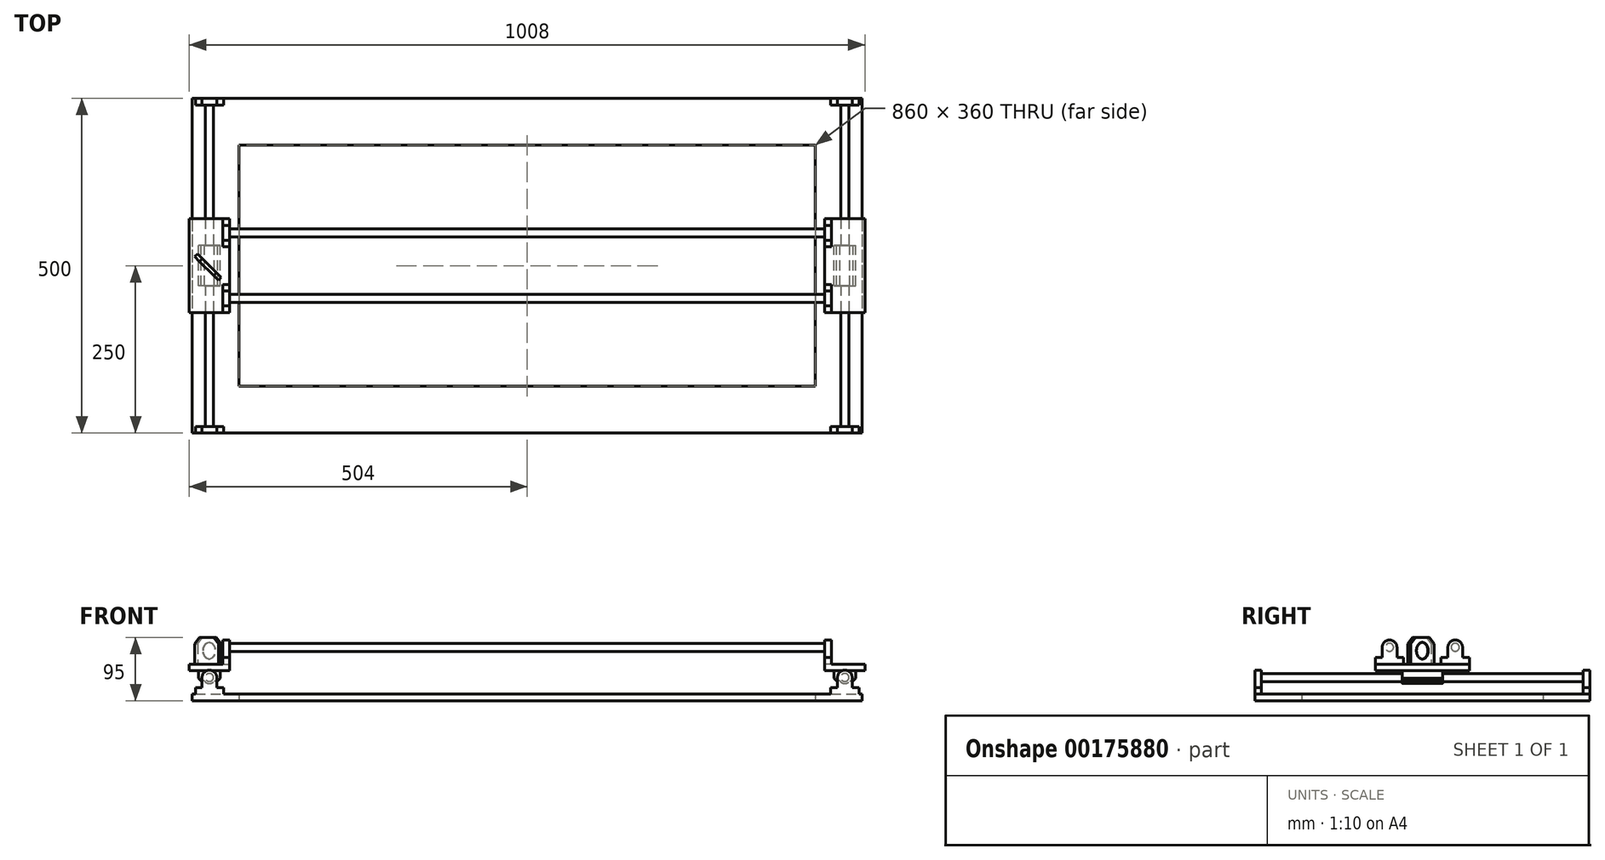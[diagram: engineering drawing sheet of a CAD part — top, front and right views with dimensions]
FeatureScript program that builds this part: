
annotation { "Feature Type Name" : "Feature", "Feature Type Description" : "" }
export const myFeature = defineFeature(function(context is Context, id is Id, definition is map)
    precondition{}
    {
        {
            var Q0;
            Q0=qCreatedBy(makeId("Top.planeOp"),FACE);
            var sketch = newSketch(context, id + "F0", { "sketchPlane" : qUnion([Q0])});
            skLineSegment(sketch, "E0.bottom", {"start": v(-500, 250) * mm, "end": v(500, 250) * mm});
            skLineSegment(sketch, "E0.top", {"start": v(-500, -250) * mm, "end": v(500, -250) * mm});
            skLineSegment(sketch, "E0.left", {"start": v(-500, 250) * mm, "end": v(-500, -250) * mm});
            skLineSegment(sketch, "E0.right", {"start": v(500, 250) * mm, "end": v(500, -250) * mm});
            skPoint(sketch, "E0.middle", {"position": v(0, 0) * mm});
            skLineSegment(sketch, "E1.0", {"start": v(-430, 180) * mm, "end": v(430, 180) * mm});
            skLineSegment(sketch, "E1.1", {"start": v(-430, 180) * mm, "end": v(-430, -180) * mm});
            skLineSegment(sketch, "E1.2", {"start": v(-430, -180) * mm, "end": v(430, -180) * mm});
            skLineSegment(sketch, "E1.3", {"start": v(430, 180) * mm, "end": v(430, -180) * mm});
            skSolve(sketch);
        }
        {
            var Q0;
            Q0=makeQuery(id+"F0.imprint","IMPRINT",FACE,{"disambiguationData":[TD([[makeQuery(id+"F0.imprint","IMPRINT",EDGE,{"derivedFrom":sQuery(id+"F0.wireOp",EDGE,"E0.bottom")}),-1.0]])]});
            extrude(context, id + "F1", {"entities" : qUnion([Q0]), "endBound" : BoundingType.SYMMETRIC, "depth" : 10 * mm});
        }
        {
            var Q0;
            Q0=makeQuery(id+"F1.opExtrude","SWEPT_FACE",FACE,{"disambiguationData":[OSD([sQuery(id+"F0.wireOp",EDGE,"E0.top")])]});
            var sketch = newSketch(context, id + "F2", { "sketchPlane" : qUnion([Q0])});
            skCircle(sketch, "E2", {"center": v(-474, 30) * mm, "radius": 6 * mm});
            skArc(sketch, "E3", {"start": v(-485, 30) * mm, "mid": v(-481.78, 37.78) * mm, "end": v(-474, 41) * mm});
            skLineSegment(sketch, "E4", {"start": v(-485, 30) * mm, "end": v(-485, 15) * mm});
            skLineSegment(sketch, "E5", {"start": v(-485, 15) * mm, "end": v(-495, 15) * mm});
            skLineSegment(sketch, "E6", {"start": v(-495, 15) * mm, "end": v(-495, 5) * mm});
            skLineSegment(sketch, "E7", {"start": v(-474, 30) * mm, "end": v(-474, 5) * mm, "construction": true});
            skArc(sketch, "E8.MirrorCS", {"start": v(-463, 30) * mm, "mid": v(-466.22, 37.78) * mm, "end": v(-474, 41) * mm});
            skLineSegment(sketch, "E9.MirrorCS", {"start": v(-463, 30) * mm, "end": v(-463, 15) * mm});
            skLineSegment(sketch, "E10.MirrorCS", {"start": v(-453, 15) * mm, "end": v(-453, 5) * mm});
            skLineSegment(sketch, "E11.MirrorCS", {"start": v(-463, 15) * mm, "end": v(-453, 15) * mm});
            skLineSegment(sketch, "E12", {"start": v(-495, 5) * mm, "end": v(-453, 5) * mm});
            skCircle(sketch, "E13.MirrorC", {"center": v(474, 30) * mm, "radius": 6 * mm});
            skArc(sketch, "E14.MirrorCS", {"start": v(463, 30) * mm, "mid": v(466.22, 37.78) * mm, "end": v(474, 41) * mm});
            skLineSegment(sketch, "E15.MirrorCS", {"start": v(453, 15) * mm, "end": v(453, 5) * mm});
            skLineSegment(sketch, "E16.MirrorCS", {"start": v(463, 30) * mm, "end": v(463, 15) * mm});
            skLineSegment(sketch, "E17.MirrorCS", {"start": v(485, 15) * mm, "end": v(495, 15) * mm});
            skLineSegment(sketch, "E18.MirrorCS", {"start": v(495, 15) * mm, "end": v(495, 5) * mm});
            skLineSegment(sketch, "E19.MirrorCS", {"start": v(485, 30) * mm, "end": v(485, 15) * mm});
            skArc(sketch, "E20.MirrorCS", {"start": v(485, 30) * mm, "mid": v(481.78, 37.78) * mm, "end": v(474, 41) * mm});
            skLineSegment(sketch, "E21.MirrorCS", {"start": v(463, 15) * mm, "end": v(453, 15) * mm});
            skLineSegment(sketch, "E22.MirrorCS", {"start": v(474, 30) * mm, "end": v(474, 5) * mm, "construction": true});
            skLineSegment(sketch, "E23.MirrorCS", {"start": v(495, 5) * mm, "end": v(453, 5) * mm});
            skSolve(sketch);
        }
        {
            var Q0;
            Q0 = qSketchRegion(id + "F2", true);
            extrude(context, id + "F3", {"entities" : qUnion([Q0]), "oppositeDirection" : true, "depth" : 10 * mm});
        }
        {
            var Q0;
            Q0=makeQuery(id+"F3.opExtrude","SWEPT_BODY",BODY,{"disambiguationData":[OSD([sQuery(id+"F2.wireOp",EDGE,"E2"),sQuery(id+"F2.wireOp",EDGE,"E3"),sQuery(id+"F2.wireOp",EDGE,"E4"),sQuery(id+"F2.wireOp",EDGE,"E5"),sQuery(id+"F2.wireOp",EDGE,"E6"),sQuery(id+"F2.wireOp",EDGE,"E8.MirrorCS"),sQuery(id+"F2.wireOp",EDGE,"E9.MirrorCS"),sQuery(id+"F2.wireOp",EDGE,"E10.MirrorCS"),sQuery(id+"F2.wireOp",EDGE,"E11.MirrorCS"),sQuery(id+"F2.wireOp",EDGE,"E12")])]});
            var Q1;
            Q1=makeQuery(id+"F3.opExtrude","SWEPT_BODY",BODY,{"disambiguationData":[OSD([sQuery(id+"F2.wireOp",EDGE,"E13.MirrorC"),sQuery(id+"F2.wireOp",EDGE,"E14.MirrorCS"),sQuery(id+"F2.wireOp",EDGE,"E15.MirrorCS"),sQuery(id+"F2.wireOp",EDGE,"E16.MirrorCS"),sQuery(id+"F2.wireOp",EDGE,"E17.MirrorCS"),sQuery(id+"F2.wireOp",EDGE,"E18.MirrorCS"),sQuery(id+"F2.wireOp",EDGE,"E19.MirrorCS"),sQuery(id+"F2.wireOp",EDGE,"E20.MirrorCS"),sQuery(id+"F2.wireOp",EDGE,"E21.MirrorCS"),sQuery(id+"F2.wireOp",EDGE,"E23.MirrorCS")])]});
            var Q2;
            Q2=qCreatedBy(makeId("Front.planeOp"),FACE);
            mirror(context, id + "F4", {"operationType" : NewBodyOperationType.ADD, "entities" : qUnion([Q0, Q1]), "mirrorPlane" : qUnion([Q2])});
        }
        {
            var Q0;
            Q0=makeQuery(id+"F4.boolean.opBoolean","MERGE",FACE,{"derivedFrom":[makeQuery(id+"F1.opExtrude","SWEPT_FACE",FACE,{"disambiguationData":[OSD([sQuery(id+"F0.wireOp",EDGE,"E0.top")])]}),makeQuery(id+"F3.opExtrude","CAP_FACE",FACE,{"disambiguationData":[OSD([sQuery(id+"F2.wireOp",EDGE,"E2"),sQuery(id+"F2.wireOp",EDGE,"E3"),sQuery(id+"F2.wireOp",EDGE,"E4"),sQuery(id+"F2.wireOp",EDGE,"E5"),sQuery(id+"F2.wireOp",EDGE,"E6"),sQuery(id+"F2.wireOp",EDGE,"E8.MirrorCS"),sQuery(id+"F2.wireOp",EDGE,"E9.MirrorCS"),sQuery(id+"F2.wireOp",EDGE,"E10.MirrorCS"),sQuery(id+"F2.wireOp",EDGE,"E11.MirrorCS"),sQuery(id+"F2.wireOp",EDGE,"E12")])],"isStart":true}),makeQuery(id+"F3.opExtrude","CAP_FACE",FACE,{"disambiguationData":[OSD([sQuery(id+"F2.wireOp",EDGE,"E13.MirrorC"),sQuery(id+"F2.wireOp",EDGE,"E14.MirrorCS"),sQuery(id+"F2.wireOp",EDGE,"E15.MirrorCS"),sQuery(id+"F2.wireOp",EDGE,"E16.MirrorCS"),sQuery(id+"F2.wireOp",EDGE,"E17.MirrorCS"),sQuery(id+"F2.wireOp",EDGE,"E18.MirrorCS"),sQuery(id+"F2.wireOp",EDGE,"E19.MirrorCS"),sQuery(id+"F2.wireOp",EDGE,"E20.MirrorCS"),sQuery(id+"F2.wireOp",EDGE,"E21.MirrorCS"),sQuery(id+"F2.wireOp",EDGE,"E23.MirrorCS")])],"isStart":true})]});
            var sketch = newSketch(context, id + "F5", { "sketchPlane" : qUnion([Q0])});
            skCircle(sketch, "E24.0", {"center": v(-474, 30) * mm, "radius": 6 * mm});
            skCircle(sketch, "E25.0", {"center": v(474, 30) * mm, "radius": 6 * mm});
            skSolve(sketch);
        }
        {
            var Q0;
            Q0 = qSketchRegion(id + "F5", true);
            var Q1;
            Q1=makeQuery(id+"F4.boolean.opBoolean","MERGE",FACE,{"derivedFrom":[makeQuery(id+"F1.opExtrude","SWEPT_FACE",FACE,{"disambiguationData":[OSD([sQuery(id+"F0.wireOp",EDGE,"E0.bottom")])]}),makeQuery(id+"F4.opPattern","COPY",FACE,{"derivedFrom":makeQuery(id+"F3.opExtrude","CAP_FACE",FACE,{"disambiguationData":[OSD([sQuery(id+"F2.wireOp",EDGE,"E2"),sQuery(id+"F2.wireOp",EDGE,"E3"),sQuery(id+"F2.wireOp",EDGE,"E4"),sQuery(id+"F2.wireOp",EDGE,"E5"),sQuery(id+"F2.wireOp",EDGE,"E6"),sQuery(id+"F2.wireOp",EDGE,"E8.MirrorCS"),sQuery(id+"F2.wireOp",EDGE,"E9.MirrorCS"),sQuery(id+"F2.wireOp",EDGE,"E10.MirrorCS"),sQuery(id+"F2.wireOp",EDGE,"E11.MirrorCS"),sQuery(id+"F2.wireOp",EDGE,"E12")])],"isStart":true}),"instanceName":"1"}),makeQuery(id+"F4.opPattern","COPY",FACE,{"derivedFrom":makeQuery(id+"F3.opExtrude","CAP_FACE",FACE,{"disambiguationData":[OSD([sQuery(id+"F2.wireOp",EDGE,"E13.MirrorC"),sQuery(id+"F2.wireOp",EDGE,"E14.MirrorCS"),sQuery(id+"F2.wireOp",EDGE,"E15.MirrorCS"),sQuery(id+"F2.wireOp",EDGE,"E16.MirrorCS"),sQuery(id+"F2.wireOp",EDGE,"E17.MirrorCS"),sQuery(id+"F2.wireOp",EDGE,"E18.MirrorCS"),sQuery(id+"F2.wireOp",EDGE,"E19.MirrorCS"),sQuery(id+"F2.wireOp",EDGE,"E20.MirrorCS"),sQuery(id+"F2.wireOp",EDGE,"E21.MirrorCS"),sQuery(id+"F2.wireOp",EDGE,"E23.MirrorCS")])],"isStart":true}),"instanceName":"1"})]});
            extrude(context, id + "F6", {"entities" : qUnion([Q0]), "operationType" : NewBodyOperationType.ADD, "endBound" : BoundingType.UP_TO_SURFACE, "oppositeDirection" : true, "endBoundEntityFace" : qUnion([Q1]), "depth" : 353 * mm});
        }
        {
            var Q0;
            Q0=qCreatedBy(makeId("Front.planeOp"),FACE);
            var sketch = newSketch(context, id + "F7", { "sketchPlane" : qUnion([Q0])});
            skCircle(sketch, "E26.0", {"center": v(-474, 30) * mm, "radius": 6 * mm, "construction": true});
            skArc(sketch, "E27", {"start": v(-466.54, 24.97) * mm, "mid": v(-469.77, 22.05) * mm, "end": v(-474, 21) * mm});
            skLineSegment(sketch, "E28", {"start": v(-466.54, 24.97) * mm, "end": v(-461.54, 24.97) * mm});
            skLineSegment(sketch, "E29", {"start": v(-461.54, 24.97) * mm, "end": v(-458, 28.5) * mm});
            skLineSegment(sketch, "E30", {"start": v(-458, 28.5) * mm, "end": v(-458, 40) * mm});
            skLineSegment(sketch, "E31", {"start": v(-458, 40) * mm, "end": v(-474, 40) * mm});
            skLineSegment(sketch, "E32", {"start": v(-474, 21) * mm, "end": v(-474, 40) * mm, "construction": true});
            skLineSegment(sketch, "E33.MirrorCS", {"start": v(-481.46, 24.97) * mm, "end": v(-486.46, 24.97) * mm});
            skLineSegment(sketch, "E34.MirrorCS", {"start": v(-486.46, 24.97) * mm, "end": v(-490, 28.5) * mm});
            skArc(sketch, "E35.MirrorCS", {"start": v(-481.46, 24.97) * mm, "mid": v(-478.23, 22.05) * mm, "end": v(-474, 21) * mm});
            skLineSegment(sketch, "E36.MirrorCS", {"start": v(-490, 28.5) * mm, "end": v(-490, 40) * mm});
            skLineSegment(sketch, "E37.MirrorCS", {"start": v(-490, 40) * mm, "end": v(-474, 40) * mm});
            skSolve(sketch);
        }
        {
            var Q0;
            Q0 = qSketchRegion(id + "F7", true);
            extrude(context, id + "F8", {"entities" : qUnion([Q0]), "endBound" : BoundingType.SYMMETRIC, "depth" : 60 * mm});
        }
        {
            var Q0;
            Q0=makeQuery(id+"F8.opExtrude","SWEPT_BODY",BODY,{"disambiguationData":[OSD([sQuery(id+"F7.wireOp",EDGE,"E27"),sQuery(id+"F7.wireOp",EDGE,"E28"),sQuery(id+"F7.wireOp",EDGE,"E29"),sQuery(id+"F7.wireOp",EDGE,"E30"),sQuery(id+"F7.wireOp",EDGE,"E31"),sQuery(id+"F7.wireOp",EDGE,"E33.MirrorCS"),sQuery(id+"F7.wireOp",EDGE,"E34.MirrorCS"),sQuery(id+"F7.wireOp",EDGE,"E35.MirrorCS"),sQuery(id+"F7.wireOp",EDGE,"E36.MirrorCS"),sQuery(id+"F7.wireOp",EDGE,"E37.MirrorCS")])]});
            var Q1;
            Q1=qCreatedBy(makeId("Right.planeOp"),FACE);
            mirror(context, id + "F9", {"operationType" : NewBodyOperationType.ADD, "entities" : qUnion([Q0]), "mirrorPlane" : qUnion([Q1])});
        }
        {
            var Q0;
            Q0=makeQuery(id+"F8.opExtrude","SWEPT_FACE",FACE,{"disambiguationData":[OSD([sQuery(id+"F7.wireOp",EDGE,"E31"),sQuery(id+"F7.wireOp",EDGE,"E37.MirrorCS")])]});
            var sketch = newSketch(context, id + "F10", { "sketchPlane" : qUnion([Q0])});
            skLineSegment(sketch, "E38.bottom", {"start": v(-504, 70) * mm, "end": v(-444, 70) * mm});
            skLineSegment(sketch, "E38.top", {"start": v(-504, -70) * mm, "end": v(-444, -70) * mm});
            skLineSegment(sketch, "E38.left", {"start": v(-504, 70) * mm, "end": v(-504, -70) * mm});
            skLineSegment(sketch, "E38.right", {"start": v(-444, 70) * mm, "end": v(-444, -70) * mm});
            skPoint(sketch, "E38.middle", {"position": v(-474, 0) * mm});
            skSolve(sketch);
        }
        {
            var Q0;
            Q0 = qSketchRegion(id + "F10", true);
            extrude(context, id + "F11", {"entities" : qUnion([Q0]), "depth" : 10 * mm});
        }
        {
            var Q0;
            Q0=makeQuery(id+"F11.opExtrude","SWEPT_BODY",BODY,{"disambiguationData":[OSD([sQuery(id+"F10.wireOp",EDGE,"E38.bottom"),sQuery(id+"F10.wireOp",EDGE,"E38.top"),sQuery(id+"F10.wireOp",EDGE,"E38.left"),sQuery(id+"F10.wireOp",EDGE,"E38.right")])]});
            var Q1;
            Q1=qCreatedBy(makeId("Right.planeOp"),FACE);
            mirror(context, id + "F12", {"operationType" : NewBodyOperationType.ADD, "entities" : qUnion([Q0]), "mirrorPlane" : qUnion([Q1])});
        }
        {
            var Q0;
            Q0=makeQuery(id+"F11.opExtrude","SWEPT_FACE",FACE,{"disambiguationData":[OSD([sQuery(id+"F10.wireOp",EDGE,"E38.right")])]});
            var sketch = newSketch(context, id + "F13", { "sketchPlane" : qUnion([Q0])});
            skLineSegment(sketch, "E39", {"start": v(28, 50) * mm, "end": v(28, 60) * mm});
            skLineSegment(sketch, "E40", {"start": v(28, 60) * mm, "end": v(38, 60) * mm});
            skLineSegment(sketch, "E41", {"start": v(38, 60) * mm, "end": v(38, 75) * mm});
            skCircle(sketch, "E42", {"center": v(49, 75) * mm, "radius": 6 * mm});
            skArc(sketch, "E43", {"start": v(38, 75) * mm, "mid": v(41.22, 82.78) * mm, "end": v(49, 86) * mm});
            skLineSegment(sketch, "E44", {"start": v(49, 86) * mm, "end": v(49, 50) * mm, "construction": true});
            skLineSegment(sketch, "E45", {"start": v(49, 50) * mm, "end": v(28, 50) * mm});
            skLineSegment(sketch, "E46.MirrorCS", {"start": v(70, 60) * mm, "end": v(60, 60) * mm});
            skLineSegment(sketch, "E47.MirrorCS", {"start": v(60, 60) * mm, "end": v(60, 75) * mm});
            skArc(sketch, "E48.MirrorCS", {"start": v(60, 75) * mm, "mid": v(56.78, 82.78) * mm, "end": v(49, 86) * mm});
            skLineSegment(sketch, "E49.MirrorCS", {"start": v(49, 50) * mm, "end": v(70, 50) * mm});
            skLineSegment(sketch, "E50.MirrorCS", {"start": v(70, 50) * mm, "end": v(70, 60) * mm});
            skSolve(sketch);
        }
        {
            var Q0;
            Q0 = qSketchRegion(id + "F13", true);
            extrude(context, id + "F14", {"entities" : qUnion([Q0]), "oppositeDirection" : true, "depth" : 10 * mm});
        }
        {
            var Q0;
            Q0=makeQuery(id+"F14.opExtrude","SWEPT_BODY",BODY,{"disambiguationData":[OSD([sQuery(id+"F13.wireOp",EDGE,"E39"),sQuery(id+"F13.wireOp",EDGE,"E40"),sQuery(id+"F13.wireOp",EDGE,"E41"),sQuery(id+"F13.wireOp",EDGE,"E42"),sQuery(id+"F13.wireOp",EDGE,"E43"),sQuery(id+"F13.wireOp",EDGE,"E45"),sQuery(id+"F13.wireOp",EDGE,"E46.MirrorCS"),sQuery(id+"F13.wireOp",EDGE,"E47.MirrorCS"),sQuery(id+"F13.wireOp",EDGE,"E48.MirrorCS"),sQuery(id+"F13.wireOp",EDGE,"E49.MirrorCS"),sQuery(id+"F13.wireOp",EDGE,"E50.MirrorCS")])]});
            var Q1;
            Q1=qCreatedBy(makeId("Front.planeOp"),FACE);
            mirror(context, id + "F15", {"entities" : qUnion([Q0]), "mirrorPlane" : qUnion([Q1])});
        }
        {
            var Q0;
            Q0=makeQuery(id+"F14.opExtrude","SWEPT_BODY",BODY,{"disambiguationData":[OSD([sQuery(id+"F13.wireOp",EDGE,"E39"),sQuery(id+"F13.wireOp",EDGE,"E40"),sQuery(id+"F13.wireOp",EDGE,"E41"),sQuery(id+"F13.wireOp",EDGE,"E42"),sQuery(id+"F13.wireOp",EDGE,"E43"),sQuery(id+"F13.wireOp",EDGE,"E45"),sQuery(id+"F13.wireOp",EDGE,"E46.MirrorCS"),sQuery(id+"F13.wireOp",EDGE,"E47.MirrorCS"),sQuery(id+"F13.wireOp",EDGE,"E48.MirrorCS"),sQuery(id+"F13.wireOp",EDGE,"E49.MirrorCS"),sQuery(id+"F13.wireOp",EDGE,"E50.MirrorCS")])]});
            var Q1;
            Q1=makeQuery(id+"F15.opPattern","COPY",BODY,{"derivedFrom":makeQuery(id+"F14.opExtrude","SWEPT_BODY",BODY,{"disambiguationData":[OSD([sQuery(id+"F13.wireOp",EDGE,"E39"),sQuery(id+"F13.wireOp",EDGE,"E40"),sQuery(id+"F13.wireOp",EDGE,"E41"),sQuery(id+"F13.wireOp",EDGE,"E42"),sQuery(id+"F13.wireOp",EDGE,"E43"),sQuery(id+"F13.wireOp",EDGE,"E45"),sQuery(id+"F13.wireOp",EDGE,"E46.MirrorCS"),sQuery(id+"F13.wireOp",EDGE,"E47.MirrorCS"),sQuery(id+"F13.wireOp",EDGE,"E48.MirrorCS"),sQuery(id+"F13.wireOp",EDGE,"E49.MirrorCS"),sQuery(id+"F13.wireOp",EDGE,"E50.MirrorCS")])]}),"instanceName":"1"});
            var Q2;
            Q2=qCreatedBy(makeId("Right.planeOp"),FACE);
            mirror(context, id + "F16", {"operationType" : NewBodyOperationType.ADD, "entities" : qUnion([Q0, Q1]), "mirrorPlane" : qUnion([Q2])});
        }
        {
            var Q0;
            Q0=makeQuery(id+"F14.opExtrude","CAP_FACE",FACE,{"disambiguationData":[OSD([sQuery(id+"F13.wireOp",EDGE,"E39"),sQuery(id+"F13.wireOp",EDGE,"E40"),sQuery(id+"F13.wireOp",EDGE,"E41"),sQuery(id+"F13.wireOp",EDGE,"E42"),sQuery(id+"F13.wireOp",EDGE,"E43"),sQuery(id+"F13.wireOp",EDGE,"E45"),sQuery(id+"F13.wireOp",EDGE,"E46.MirrorCS"),sQuery(id+"F13.wireOp",EDGE,"E47.MirrorCS"),sQuery(id+"F13.wireOp",EDGE,"E48.MirrorCS"),sQuery(id+"F13.wireOp",EDGE,"E49.MirrorCS"),sQuery(id+"F13.wireOp",EDGE,"E50.MirrorCS")])],"isStart":false});
            var sketch = newSketch(context, id + "F17", { "sketchPlane" : qUnion([Q0])});
            skCircle(sketch, "E51.0", {"center": v(-49, 75) * mm, "radius": 6 * mm});
            skCircle(sketch, "E52.0", {"center": v(49, 75) * mm, "radius": 6 * mm});
            skSolve(sketch);
        }
        {
            var Q0;
            Q0 = qSketchRegion(id + "F17", true);
            var Q1;
            Q1=makeQuery(id+"F16.opPattern","COPY",FACE,{"derivedFrom":makeQuery(id+"F14.opExtrude","CAP_FACE",FACE,{"disambiguationData":[OSD([sQuery(id+"F13.wireOp",EDGE,"E39"),sQuery(id+"F13.wireOp",EDGE,"E40"),sQuery(id+"F13.wireOp",EDGE,"E41"),sQuery(id+"F13.wireOp",EDGE,"E42"),sQuery(id+"F13.wireOp",EDGE,"E43"),sQuery(id+"F13.wireOp",EDGE,"E45"),sQuery(id+"F13.wireOp",EDGE,"E46.MirrorCS"),sQuery(id+"F13.wireOp",EDGE,"E47.MirrorCS"),sQuery(id+"F13.wireOp",EDGE,"E48.MirrorCS"),sQuery(id+"F13.wireOp",EDGE,"E49.MirrorCS"),sQuery(id+"F13.wireOp",EDGE,"E50.MirrorCS")])],"isStart":false}),"instanceName":"1"});
            extrude(context, id + "F18", {"entities" : qUnion([Q0]), "operationType" : NewBodyOperationType.ADD, "endBound" : BoundingType.UP_TO_SURFACE, "oppositeDirection" : true, "endBoundEntityFace" : qUnion([Q1]), "depth" : 25 * mm});
        }
        {
            var Q0;
            Q0=makeQuery(id+"F11.opExtrude","CAP_FACE",FACE,{"disambiguationData":[OSD([sQuery(id+"F10.wireOp",EDGE,"E38.bottom"),sQuery(id+"F10.wireOp",EDGE,"E38.top"),sQuery(id+"F10.wireOp",EDGE,"E38.left"),sQuery(id+"F10.wireOp",EDGE,"E38.right")])],"isStart":false});
            var sketch = newSketch(context, id + "F19", { "sketchPlane" : qUnion([Q0])});
            skLineSegment(sketch, "E53", {"start": v(-491.68, 17.68) * mm, "end": v(-456.32, -17.68) * mm});
            skLineSegment(sketch, "E54", {"start": v(-491.68, 17.68) * mm, "end": v(-495.92, 13.44) * mm});
            skLineSegment(sketch, "E55", {"start": v(-460.56, -21.92) * mm, "end": v(-495.92, 13.44) * mm});
            skLineSegment(sketch, "E56", {"start": v(-460.56, -21.92) * mm, "end": v(-456.32, -17.68) * mm});
            skPoint(sketch, "E57", {"position": v(-474, 0) * mm});
            skSolve(sketch);
        }
        {
            var Q0;
            Q0 = qSketchRegion(id + "F19", true);
            extrude(context, id + "F20", {"entities" : qUnion([Q0]), "operationType" : NewBodyOperationType.ADD, "depth" : 40 * mm});
        }
        {
            var Q0;
            Q0=makeQuery(id+"F20.opExtrude","SWEPT_FACE",FACE,{"disambiguationData":[OSD([sQuery(id+"F19.wireOp",EDGE,"E53")])]});
            var sketch = newSketch(context, id + "F21", { "sketchPlane" : qUnion([Q0])});
            skCircle(sketch, "E58", {"center": v(335.17, 70) * mm, "radius": 12.5 * mm});
            skSolve(sketch);
        }
        {
            var Q0;
            Q0=makeQuery(id+"F20.opExtrude","CAP_EDGE",EDGE,{"disambiguationData":[OSD([sQuery(id+"F19.wireOp",EDGE,"E56")])],"isStart":false});
            var Q1;
            Q1=makeQuery(id+"F20.opExtrude","CAP_EDGE",EDGE,{"disambiguationData":[OSD([sQuery(id+"F19.wireOp",EDGE,"E54")])],"isStart":false});
            chamfer(context, id + "F22", {"entities" : qUnion([Q0, Q1]), "width" : 10 * mm, "tangentPropagation" : true});
        }
        {
            var Q0;
            Q0 = qSketchRegion(id + "F21", true);
            extrude(context, id + "F23", {"entities" : qUnion([Q0]), "operationType" : NewBodyOperationType.REMOVE, "oppositeDirection" : true, "depth" : 1 * mm});
        }
    });
